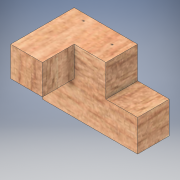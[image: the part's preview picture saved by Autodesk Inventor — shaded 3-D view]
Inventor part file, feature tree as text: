
AUTODESK INVENTOR PART (.ipt)
format: ipt  version: 2018 (Build 220112000, 112)  size: 150,528 bytes
history: native  units: in
note: dims shown in document units (in); Inventor stores cm internally (conversion verified against a paired STEP export)
features: sketch x5, extrude x4
ambient origin geometry x8: Origin, YZ Plane, XZ Plane, XY Plane, X Axis, Y Axis, Z Axis, Center Point
bodies: Solid1 (feature_tree)
feature tree (9):
  extrude  "Extrusion1"  Depth=2.0in
  extrude  "Extrusion2"  Depth=1.0in
  sketch  "Sketch3"  dims[d5=2.0in d6=0.0in d7=1.0in]
  extrude  "Extrusion3"  Depth=1.0in
  extrude  "Extrusion4"  Depth=1.0in
  sketch  "Sketch1"  dims[d0=3.0in d1=2.0in]
  sketch  "Sketch2"  dims[d2=2.0in d3=0.0in d4=1.0in]
  sketch  "Sketch4"  dims[d8=2.0in d9=0.0in d10=1.0in]
  sketch  "Sketch5"  dims[d11=1.0in d12=2.0in d13=0.0in]
